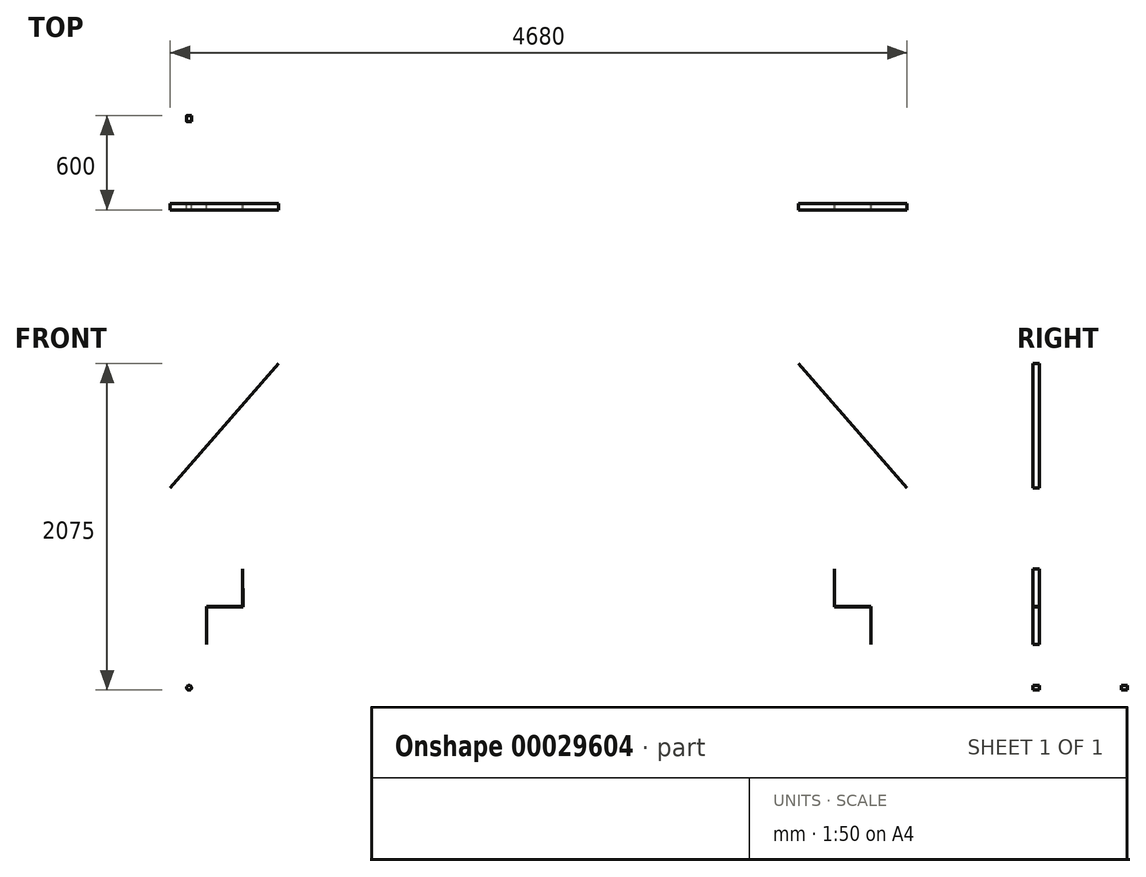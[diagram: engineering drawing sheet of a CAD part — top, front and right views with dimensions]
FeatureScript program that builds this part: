
annotation { "Feature Type Name" : "Feature", "Feature Type Description" : "" }
export const myFeature = defineFeature(function(context is Context, id is Id, definition is map)
    precondition{}
    {
        {
            var Q0;
            Q0=qCreatedBy(makeId("Top.planeOp"),FACE);
            var sketch = newSketch(context, id + "F0", { "sketchPlane" : qUnion([Q0])});
            skLineSegment(sketch, "E0.rect.bottom", {"start": v(1650, 400) * mm, "end": v(-1650, 400) * mm});
            skLineSegment(sketch, "E0.rect.top", {"start": v(1650, -400) * mm, "end": v(-1650, -400) * mm});
            skLineSegment(sketch, "E0.rect.left", {"start": v(1650, 400) * mm, "end": v(1650, -400) * mm});
            skLineSegment(sketch, "E0.rect.right", {"start": v(-1650, 400) * mm, "end": v(-1650, -400) * mm});
            skPoint(sketch, "E0.rect.middle", {"position": v(0, 0) * mm});
            skLineSegment(sketch, "E1.rect.bottom", {"start": v(1610, 360) * mm, "end": v(-1610, 360) * mm});
            skLineSegment(sketch, "E1.rect.top", {"start": v(1610, -360) * mm, "end": v(-1610, -360) * mm});
            skLineSegment(sketch, "E1.rect.left", {"start": v(1610, 360) * mm, "end": v(1610, -360) * mm});
            skLineSegment(sketch, "E1.rect.right", {"start": v(-1610, 360) * mm, "end": v(-1610, -360) * mm});
            skLineSegment(sketch, "E2", {"start": v(0, 360) * mm, "end": v(0, -360) * mm, "construction": true});
            skLineSegment(sketch, "E3", {"start": v(20, 360) * mm, "end": v(20, -360) * mm});
            skLineSegment(sketch, "E4", {"start": v(-20, 360) * mm, "end": v(-20, -360) * mm});
            skLineSegment(sketch, "E5", {"start": v(1610, -20) * mm, "end": v(-1610, -20) * mm});
            skLineSegment(sketch, "E6.0", {"start": v(1610, 20) * mm, "end": v(-1610, 20) * mm});
            skLineSegment(sketch, "E7", {"start": v(0, 0) * mm, "end": v(1610, 0) * mm, "construction": true});
            skLineSegment(sketch, "E8", {"start": v(0, 0) * mm, "end": v(-1610, 0) * mm, "construction": true});
            skLineSegment(sketch, "E9", {"start": v(805, 0) * mm, "end": v(805, 360) * mm, "construction": true});
            skLineSegment(sketch, "E10", {"start": v(805, 0) * mm, "end": v(805, -360) * mm, "construction": true});
            skLineSegment(sketch, "E11", {"start": v(825, 360) * mm, "end": v(825, -360) * mm});
            skLineSegment(sketch, "E12", {"start": v(785, 360) * mm, "end": v(785, -360) * mm});
            skLineSegment(sketch, "E13.MirrorCS", {"start": v(-785, 360) * mm, "end": v(-785, -360) * mm});
            skLineSegment(sketch, "E14.MirrorCS", {"start": v(-825, 360) * mm, "end": v(-825, -360) * mm});
            skSolve(sketch);
        }
        {
            var Q0;
            Q0=makeQuery(id+"F0.imprint","IMPRINT",FACE,{"disambiguationData":[TD([[makeQuery(id+"F0.imprint","IMPRINT",EDGE,{"derivedFrom":sQuery(id+"F0.wireOp",EDGE,"E0.rect.bottom")}),1.0]])]});
            var Q1;
            {var subQ3=sQuery(id+"F0.wireOp",EDGE,"E1.rect.bottom");var subQ5=sQuery(id+"F0.wireOp",EDGE,"E13.MirrorCS");var subQ7=makeQuery(id+"F0.imprint","INTERSECT",VERTEX,{"derivedFrom":[subQ3,subQ5]});Q1=makeQuery(id+"F0.imprint","IMPRINT",FACE,{"disambiguationData":[TD([[makeQuery(id+"F0.imprint","IMPRINT",EDGE,{"disambiguationData":[TD([[subQ7,-1.0]])],"derivedFrom":subQ3}),1.0]])]});}
            var Q2;
            {var subQ3=sQuery(id+"F0.wireOp",EDGE,"E5");var subQ5=sQuery(id+"F0.wireOp",EDGE,"E13.MirrorCS");var subQ7=makeQuery(id+"F0.imprint","INTERSECT",VERTEX,{"derivedFrom":[subQ3,subQ5]});Q2=makeQuery(id+"F0.imprint","IMPRINT",FACE,{"disambiguationData":[TD([[makeQuery(id+"F0.imprint","IMPRINT",EDGE,{"disambiguationData":[TD([[subQ7,-1.0]])],"derivedFrom":subQ3}),-1.0]])]});}
            var Q3;
            {var subQ0=sQuery(id+"F0.wireOp",EDGE,"E13.MirrorCS");var subQ3=sQuery(id+"F0.wireOp",EDGE,"E1.rect.top");var subQ4=makeQuery(id+"F0.imprint","INTERSECT",VERTEX,{"derivedFrom":[subQ3,subQ0]});Q3=makeQuery(id+"F0.imprint","IMPRINT",FACE,{"disambiguationData":[TD([[makeQuery(id+"F0.imprint","IMPRINT",EDGE,{"disambiguationData":[TD([[subQ4,-1.0]])],"derivedFrom":subQ3}),-1.0]])]});}
            var Q4;
            {var subQ3=sQuery(id+"F0.wireOp",EDGE,"E5");var subQ5=sQuery(id+"F0.wireOp",EDGE,"E1.rect.right");var subQ7=makeQuery(id+"F0.imprint","INTERSECT",VERTEX,{"derivedFrom":[subQ5,subQ3]});Q4=makeQuery(id+"F0.imprint","IMPRINT",FACE,{"disambiguationData":[TD([[makeQuery(id+"F0.imprint","IMPRINT",EDGE,{"disambiguationData":[TD([[subQ7,1.0]])],"derivedFrom":subQ5}),1.0]])]});}
            var Q5;
            {var subQ0=sQuery(id+"F0.wireOp",EDGE,"E6.0");var subQ3=sQuery(id+"F0.wireOp",EDGE,"E4");var subQ4=makeQuery(id+"F0.imprint","INTERSECT",VERTEX,{"derivedFrom":[subQ3,subQ0]});Q5=makeQuery(id+"F0.imprint","IMPRINT",FACE,{"disambiguationData":[TD([[makeQuery(id+"F0.imprint","IMPRINT",EDGE,{"disambiguationData":[TD([[subQ4,-1.0]])],"derivedFrom":subQ3}),-1.0]])]});}
            var Q6;
            {var subQ3=sQuery(id+"F0.wireOp",EDGE,"E3");var subQ5=sQuery(id+"F0.wireOp",EDGE,"E1.rect.top");var subQ6=makeQuery(id+"F0.imprint","INTERSECT",VERTEX,{"derivedFrom":[subQ5,subQ3]});Q6=makeQuery(id+"F0.imprint","IMPRINT",FACE,{"disambiguationData":[TD([[makeQuery(id+"F0.imprint","IMPRINT",EDGE,{"disambiguationData":[TD([[subQ6,-1.0]])],"derivedFrom":subQ5}),-1.0]])]});}
            var Q7;
            {var subQ3=sQuery(id+"F0.wireOp",EDGE,"E1.rect.bottom");var subQ5=sQuery(id+"F0.wireOp",EDGE,"E3");var subQ7=makeQuery(id+"F0.imprint","INTERSECT",VERTEX,{"derivedFrom":[subQ3,subQ5]});Q7=makeQuery(id+"F0.imprint","IMPRINT",FACE,{"disambiguationData":[TD([[makeQuery(id+"F0.imprint","IMPRINT",EDGE,{"disambiguationData":[TD([[subQ7,-1.0]])],"derivedFrom":subQ3}),1.0]])]});}
            var Q8;
            {var subQ3=sQuery(id+"F0.wireOp",EDGE,"E5");var subQ5=sQuery(id+"F0.wireOp",EDGE,"E1.rect.left");var subQ6=makeQuery(id+"F0.imprint","INTERSECT",VERTEX,{"derivedFrom":[subQ5,subQ3]});Q8=makeQuery(id+"F0.imprint","IMPRINT",FACE,{"disambiguationData":[TD([[makeQuery(id+"F0.imprint","IMPRINT",EDGE,{"disambiguationData":[TD([[subQ6,1.0]])],"derivedFrom":subQ5}),-1.0]])]});}
            var Q9;
            {var subQ3=sQuery(id+"F0.wireOp",EDGE,"E1.rect.top");var subQ5=sQuery(id+"F0.wireOp",EDGE,"E11");var subQ7=makeQuery(id+"F0.imprint","INTERSECT",VERTEX,{"derivedFrom":[subQ3,subQ5]});Q9=makeQuery(id+"F0.imprint","IMPRINT",FACE,{"disambiguationData":[TD([[makeQuery(id+"F0.imprint","IMPRINT",EDGE,{"disambiguationData":[TD([[subQ7,-1.0]])],"derivedFrom":subQ3}),-1.0]])]});}
            var Q10;
            {var subQ1=sQuery(id+"F0.wireOp",EDGE,"E6.0");var subQ5=sQuery(id+"F0.wireOp",EDGE,"E3");var subQ6=makeQuery(id+"F0.imprint","INTERSECT",VERTEX,{"derivedFrom":[subQ5,subQ1]});Q10=makeQuery(id+"F0.imprint","IMPRINT",FACE,{"disambiguationData":[TD([[makeQuery(id+"F0.imprint","IMPRINT",EDGE,{"disambiguationData":[TD([[subQ6,-1.0]])],"derivedFrom":subQ5}),1.0]])]});}
            var Q11;
            {var subQ3=sQuery(id+"F0.wireOp",EDGE,"E1.rect.bottom");var subQ5=sQuery(id+"F0.wireOp",EDGE,"E11");var subQ7=makeQuery(id+"F0.imprint","INTERSECT",VERTEX,{"derivedFrom":[subQ3,subQ5]});Q11=makeQuery(id+"F0.imprint","IMPRINT",FACE,{"disambiguationData":[TD([[makeQuery(id+"F0.imprint","IMPRINT",EDGE,{"disambiguationData":[TD([[subQ7,-1.0]])],"derivedFrom":subQ3}),1.0]])]});}
            var Q12;
            {var subQ0=sQuery(id+"F0.wireOp",EDGE,"E11");var subQ3=sQuery(id+"F0.wireOp",EDGE,"E5");var subQ4=makeQuery(id+"F0.imprint","INTERSECT",VERTEX,{"derivedFrom":[subQ3,subQ0]});Q12=makeQuery(id+"F0.imprint","IMPRINT",FACE,{"disambiguationData":[TD([[makeQuery(id+"F0.imprint","IMPRINT",EDGE,{"disambiguationData":[TD([[subQ4,-1.0]])],"derivedFrom":subQ3}),-1.0]])]});}
            var Q13;
            {var subQ3=sQuery(id+"F0.wireOp",EDGE,"E3");var subQ5=sQuery(id+"F0.wireOp",EDGE,"E6.0");var subQ7=makeQuery(id+"F0.imprint","INTERSECT",VERTEX,{"derivedFrom":[subQ3,subQ5]});Q13=makeQuery(id+"F0.imprint","IMPRINT",FACE,{"disambiguationData":[TD([[makeQuery(id+"F0.imprint","IMPRINT",EDGE,{"disambiguationData":[TD([[subQ7,-1.0]])],"derivedFrom":subQ3}),-1.0]])]});}
            extrude(context, id + "F1", {"entities" : qUnion([Q0, Q1, Q2, Q3, Q4, Q5, Q6, Q7, Q8, Q9, Q10, Q11, Q12, Q13]), "depth" : 25 * mm});
        }
        {
            var Q0;
            Q0=makeQuery(id+"F1.opExtrude","CAP_FACE",FACE,{"disambiguationData":[OSD([sQuery(id+"F0.wireOp",EDGE,"E0.rect.bottom"),sQuery(id+"F0.wireOp",EDGE,"E0.rect.top"),sQuery(id+"F0.wireOp",EDGE,"E0.rect.left"),sQuery(id+"F0.wireOp",EDGE,"E0.rect.right"),sQuery(id+"F0.wireOp",EDGE,"E1.rect.bottom"),sQuery(id+"F0.wireOp",EDGE,"E1.rect.top"),sQuery(id+"F0.wireOp",EDGE,"E1.rect.left"),sQuery(id+"F0.wireOp",EDGE,"E1.rect.right"),sQuery(id+"F0.wireOp",EDGE,"E3"),sQuery(id+"F0.wireOp",EDGE,"E4"),sQuery(id+"F0.wireOp",EDGE,"E5"),sQuery(id+"F0.wireOp",EDGE,"E6.0"),sQuery(id+"F0.wireOp",EDGE,"E11"),sQuery(id+"F0.wireOp",EDGE,"E12"),sQuery(id+"F0.wireOp",EDGE,"E13.MirrorCS"),sQuery(id+"F0.wireOp",EDGE,"E14.MirrorCS")])],"isStart":false});
            var sketch = newSketch(context, id + "F2", { "sketchPlane" : qUnion([Q0])});
            skLineSegment(sketch, "E15.bottom", {"start": v(-1650, 400) * mm, "end": v(-1610, 400) * mm});
            skLineSegment(sketch, "E15.top", {"start": v(-1650, 360) * mm, "end": v(-1610, 360) * mm});
            skLineSegment(sketch, "E15.left", {"start": v(-1650, 400) * mm, "end": v(-1650, 360) * mm});
            skLineSegment(sketch, "E15.right", {"start": v(-1610, 400) * mm, "end": v(-1610, 360) * mm});
            skLineSegment(sketch, "E16.bottom", {"start": v(-1650, -400) * mm, "end": v(-1610, -400) * mm});
            skLineSegment(sketch, "E16.top", {"start": v(-1650, -360) * mm, "end": v(-1610, -360) * mm});
            skLineSegment(sketch, "E16.left", {"start": v(-1650, -400) * mm, "end": v(-1650, -360) * mm});
            skLineSegment(sketch, "E16.right", {"start": v(-1610, -400) * mm, "end": v(-1610, -360) * mm});
            skLineSegment(sketch, "E17.bottom", {"start": v(-825, -360) * mm, "end": v(-785, -360) * mm});
            skLineSegment(sketch, "E17.top", {"start": v(-825, -400) * mm, "end": v(-785, -400) * mm});
            skLineSegment(sketch, "E17.left", {"start": v(-825, -360) * mm, "end": v(-825, -400) * mm});
            skLineSegment(sketch, "E17.right", {"start": v(-785, -360) * mm, "end": v(-785, -400) * mm});
            skLineSegment(sketch, "E18.bottom", {"start": v(-20, -360) * mm, "end": v(20, -360) * mm});
            skLineSegment(sketch, "E18.top", {"start": v(-20, -400) * mm, "end": v(20, -400) * mm});
            skLineSegment(sketch, "E18.left", {"start": v(-20, -360) * mm, "end": v(-20, -400) * mm});
            skLineSegment(sketch, "E18.right", {"start": v(20, -360) * mm, "end": v(20, -400) * mm});
            skPoint(sketch, "E19.oppositeSnap0", {"position": v(20, 190) * mm});
            skLineSegment(sketch, "E19.bottom", {"start": v(-20, 360) * mm, "end": v(20, 360) * mm});
            skLineSegment(sketch, "E19.top", {"start": v(-20, 400) * mm, "end": v(20, 400) * mm});
            skLineSegment(sketch, "E19.left", {"start": v(-20, 360) * mm, "end": v(-20, 400) * mm});
            skLineSegment(sketch, "E19.right", {"start": v(20, 360) * mm, "end": v(20, 400) * mm});
            skLineSegment(sketch, "E20.bottom", {"start": v(-825, 360) * mm, "end": v(-785, 360) * mm});
            skLineSegment(sketch, "E20.top", {"start": v(-825, 400) * mm, "end": v(-785, 400) * mm});
            skLineSegment(sketch, "E20.left", {"start": v(-825, 360) * mm, "end": v(-825, 400) * mm});
            skLineSegment(sketch, "E20.right", {"start": v(-785, 360) * mm, "end": v(-785, 400) * mm});
            skLineSegment(sketch, "E21.bottom", {"start": v(785, 360) * mm, "end": v(825, 360) * mm});
            skLineSegment(sketch, "E21.top", {"start": v(785, 400) * mm, "end": v(825, 400) * mm});
            skLineSegment(sketch, "E21.left", {"start": v(785, 360) * mm, "end": v(785, 400) * mm});
            skLineSegment(sketch, "E21.right", {"start": v(825, 360) * mm, "end": v(825, 400) * mm});
            skLineSegment(sketch, "E22.bottom", {"start": v(785, -360) * mm, "end": v(825, -360) * mm});
            skLineSegment(sketch, "E22.top", {"start": v(785, -400) * mm, "end": v(825, -400) * mm});
            skLineSegment(sketch, "E22.left", {"start": v(785, -360) * mm, "end": v(785, -400) * mm});
            skLineSegment(sketch, "E22.right", {"start": v(825, -360) * mm, "end": v(825, -400) * mm});
            skLineSegment(sketch, "E23.bottom", {"start": v(1610, -360) * mm, "end": v(1650, -360) * mm});
            skLineSegment(sketch, "E23.top", {"start": v(1610, -400) * mm, "end": v(1650, -400) * mm});
            skLineSegment(sketch, "E23.left", {"start": v(1610, -360) * mm, "end": v(1610, -400) * mm});
            skLineSegment(sketch, "E23.right", {"start": v(1650, -360) * mm, "end": v(1650, -400) * mm});
            skLineSegment(sketch, "E24.bottom", {"start": v(1610, 360) * mm, "end": v(1650, 360) * mm});
            skLineSegment(sketch, "E24.top", {"start": v(1610, 400) * mm, "end": v(1650, 400) * mm});
            skLineSegment(sketch, "E24.left", {"start": v(1610, 360) * mm, "end": v(1610, 400) * mm});
            skLineSegment(sketch, "E24.right", {"start": v(1650, 360) * mm, "end": v(1650, 400) * mm});
            skLineSegment(sketch, "E25.bottom", {"start": v(-1650, -160) * mm, "end": v(-1610, -160) * mm});
            skLineSegment(sketch, "E25.top", {"start": v(-1650, -200) * mm, "end": v(-1610, -200) * mm});
            skLineSegment(sketch, "E25.left", {"start": v(-1650, -160) * mm, "end": v(-1650, -200) * mm});
            skLineSegment(sketch, "E25.right", {"start": v(-1610, -160) * mm, "end": v(-1610, -200) * mm});
            skLineSegment(sketch, "E26.MirrorCS", {"start": v(1650, -200) * mm, "end": v(1610, -200) * mm});
            skLineSegment(sketch, "E27.MirrorCS", {"start": v(1650, -160) * mm, "end": v(1650, -200) * mm});
            skLineSegment(sketch, "E28.MirrorCS", {"start": v(1650, -160) * mm, "end": v(1610, -160) * mm});
            skLineSegment(sketch, "E29.MirrorCS", {"start": v(1610, -160) * mm, "end": v(1610, -200) * mm});
            skSolve(sketch);
        }
        {
            var Q0;
            Q0=makeQuery(id+"F2.imprint","IMPRINT",FACE,{"disambiguationData":[TD([[makeQuery(id+"F2.imprint","IMPRINT",EDGE,{"derivedFrom":sQuery(id+"F2.wireOp",EDGE,"E15.bottom")}),1.0]])]});
            var Q1;
            Q1=makeQuery(id+"F2.imprint","IMPRINT",FACE,{"disambiguationData":[TD([[makeQuery(id+"F2.imprint","IMPRINT",EDGE,{"derivedFrom":sQuery(id+"F2.wireOp",EDGE,"E24.bottom")}),1.0]])]});
            var Q2;
            Q2=makeQuery(id+"F2.imprint","IMPRINT",FACE,{"disambiguationData":[TD([[makeQuery(id+"F2.imprint","IMPRINT",EDGE,{"derivedFrom":sQuery(id+"F2.wireOp",EDGE,"E26.MirrorCS")}),-1.0]])]});
            var Q3;
            Q3=makeQuery(id+"F2.imprint","IMPRINT",FACE,{"disambiguationData":[TD([[makeQuery(id+"F2.imprint","IMPRINT",EDGE,{"derivedFrom":sQuery(id+"F2.wireOp",EDGE,"E25.bottom")}),-1.0]])]});
            extrude(context, id + "F3", {"entities" : qUnion([Q0, Q1, Q2, Q3]), "operationType" : NewBodyOperationType.ADD, "depth" : 1000 * mm, "hasSecondDirection" : true, "secondDirectionOppositeDirection" : true, "secondDirectionDepth" : 1040 * mm});
        }
        {
            var Q0;
            Q0=makeQuery(id+"F2.imprint","IMPRINT",FACE,{"disambiguationData":[TD([[makeQuery(id+"F2.imprint","IMPRINT",EDGE,{"derivedFrom":sQuery(id+"F2.wireOp",EDGE,"E17.bottom")}),-1.0]])]});
            var Q1;
            Q1=makeQuery(id+"F2.imprint","IMPRINT",FACE,{"disambiguationData":[TD([[makeQuery(id+"F2.imprint","IMPRINT",EDGE,{"derivedFrom":sQuery(id+"F2.wireOp",EDGE,"E19.bottom")}),1.0]])]});
            var Q2;
            Q2=makeQuery(id+"F2.imprint","IMPRINT",FACE,{"disambiguationData":[TD([[makeQuery(id+"F2.imprint","IMPRINT",EDGE,{"derivedFrom":sQuery(id+"F2.wireOp",EDGE,"E18.bottom")}),-1.0]])]});
            var Q3;
            Q3=makeQuery(id+"F2.imprint","IMPRINT",FACE,{"disambiguationData":[TD([[makeQuery(id+"F2.imprint","IMPRINT",EDGE,{"derivedFrom":sQuery(id+"F2.wireOp",EDGE,"E20.bottom")}),1.0]])]});
            var Q4;
            Q4=makeQuery(id+"F2.imprint","IMPRINT",FACE,{"disambiguationData":[TD([[makeQuery(id+"F2.imprint","IMPRINT",EDGE,{"derivedFrom":sQuery(id+"F2.wireOp",EDGE,"E21.bottom")}),1.0]])]});
            var Q5;
            Q5=makeQuery(id+"F2.imprint","IMPRINT",FACE,{"disambiguationData":[TD([[makeQuery(id+"F2.imprint","IMPRINT",EDGE,{"derivedFrom":sQuery(id+"F2.wireOp",EDGE,"E22.bottom")}),-1.0]])]});
            var Q6;
            Q6=makeQuery(id+"F2.imprint","IMPRINT",FACE,{"disambiguationData":[TD([[makeQuery(id+"F2.imprint","IMPRINT",EDGE,{"derivedFrom":sQuery(id+"F2.wireOp",EDGE,"E16.bottom")}),-1.0]])]});
            var Q7;
            Q7=makeQuery(id+"F2.imprint","IMPRINT",FACE,{"disambiguationData":[TD([[makeQuery(id+"F2.imprint","IMPRINT",EDGE,{"derivedFrom":sQuery(id+"F2.wireOp",EDGE,"E23.bottom")}),-1.0]])]});
            extrude(context, id + "F4", {"entities" : qUnion([Q0, Q1, Q2, Q3, Q4, Q5, Q6, Q7]), "operationType" : NewBodyOperationType.ADD, "depth" : 1000 * mm});
        }
        {
            var Q0;
            Q0=makeQuery(id+"F4.boolean.opBoolean","MERGE",FACE,{"derivedFrom":[makeQuery(id+"F3.boolean.opBoolean","MERGE",FACE,{"derivedFrom":[makeQuery(id+"F1.opExtrude","SWEPT_FACE",FACE,{"disambiguationData":[OSD([sQuery(id+"F0.wireOp",EDGE,"E0.rect.left")])]}),makeQuery(id+"F3.opExtrude","SWEPT_FACE",FACE,{"disambiguationData":[OSD([sQuery(id+"F2.wireOp",EDGE,"E24.right")])]}),makeQuery(id+"F3.opExtrude","SWEPT_FACE",FACE,{"disambiguationData":[OSD([sQuery(id+"F2.wireOp",EDGE,"E27.MirrorCS")])]})]}),makeQuery(id+"F4.opExtrude","SWEPT_FACE",FACE,{"disambiguationData":[OSD([sQuery(id+"F2.wireOp",EDGE,"E23.right")])]})]});
            var sketch = newSketch(context, id + "F5", { "sketchPlane" : qUnion([Q0])});
            skLineSegment(sketch, "E30.bottom", {"start": v(-400, 1025) * mm, "end": v(-360, 1025) * mm});
            skLineSegment(sketch, "E30.top", {"start": v(-400, 1065) * mm, "end": v(-360, 1065) * mm});
            skLineSegment(sketch, "E30.left", {"start": v(-400, 1025) * mm, "end": v(-400, 1065) * mm});
            skLineSegment(sketch, "E30.right", {"start": v(-360, 1025) * mm, "end": v(-360, 1065) * mm});
            skLineSegment(sketch, "E31.MirrorCS", {"start": v(400, 1025) * mm, "end": v(360, 1025) * mm});
            skLineSegment(sketch, "E32.MirrorCS", {"start": v(360, 1025) * mm, "end": v(360, 1065) * mm});
            skLineSegment(sketch, "E33.MirrorCS", {"start": v(400, 1065) * mm, "end": v(360, 1065) * mm});
            skLineSegment(sketch, "E34.MirrorCS", {"start": v(400, 1025) * mm, "end": v(400, 1065) * mm});
            skSolve(sketch);
        }
        {
            var Q0;
            Q0 = qSketchRegion(id + "F5", true);
            extrude(context, id + "F6", {"entities" : qUnion([Q0]), "operationType" : NewBodyOperationType.ADD, "oppositeDirection" : true, "depth" : 3300 * mm});
        }
        {
            var Q0;
            Q0=makeQuery(id+"F3.opExtrude","CAP_FACE",FACE,{"disambiguationData":[OSD([sQuery(id+"F2.wireOp",EDGE,"E15.bottom"),sQuery(id+"F2.wireOp",EDGE,"E15.top"),sQuery(id+"F2.wireOp",EDGE,"E15.left"),sQuery(id+"F2.wireOp",EDGE,"E15.right")])],"isStart":true});
            var sketch = newSketch(context, id + "F7", { "sketchPlane" : qUnion([Q0])});
            skLineSegment(sketch, "E35.bottom", {"start": v(-1610, -400) * mm, "end": v(-2340, -400) * mm});
            skLineSegment(sketch, "E35.top", {"start": v(-1610, 200) * mm, "end": v(-2340, 200) * mm});
            skLineSegment(sketch, "E35.left", {"start": v(-1610, -400) * mm, "end": v(-1610, 200) * mm});
            skLineSegment(sketch, "E35.right", {"start": v(-2340, -400) * mm, "end": v(-2340, 200) * mm});
            skLineSegment(sketch, "E36.bottom", {"start": v(-1650, -360) * mm, "end": v(-2300, -360) * mm});
            skLineSegment(sketch, "E36.top", {"start": v(-1650, 160) * mm, "end": v(-2300, 160) * mm});
            skLineSegment(sketch, "E36.left", {"start": v(-1650, -360) * mm, "end": v(-1650, 160) * mm});
            skLineSegment(sketch, "E36.right", {"start": v(-2300, -360) * mm, "end": v(-2300, 160) * mm});
            skLineSegment(sketch, "E37.MirrorCS", {"start": v(1610, -400) * mm, "end": v(1610, 200) * mm});
            skLineSegment(sketch, "E38.MirrorCS", {"start": v(1650, -360) * mm, "end": v(1650, 160) * mm});
            skLineSegment(sketch, "E39.MirrorCS", {"start": v(1610, 200) * mm, "end": v(2340, 200) * mm});
            skLineSegment(sketch, "E40.MirrorCS", {"start": v(1650, 160) * mm, "end": v(2300, 160) * mm});
            skLineSegment(sketch, "E41.MirrorCS", {"start": v(2300, -360) * mm, "end": v(2300, 160) * mm});
            skLineSegment(sketch, "E42.MirrorCS", {"start": v(2340, -400) * mm, "end": v(2340, 200) * mm});
            skLineSegment(sketch, "E43.MirrorCS", {"start": v(1610, -400) * mm, "end": v(2340, -400) * mm});
            skLineSegment(sketch, "E44.MirrorCS", {"start": v(1650, -360) * mm, "end": v(2300, -360) * mm});
            skSolve(sketch);
        }
        {
            var Q0;
            {var subQ1=makeQuery(id+"F3.opExtrude","CAP_EDGE",EDGE,{"disambiguationData":[OSD([sQuery(id+"F2.wireOp",EDGE,"E15.top")])],"isStart":true});Q0=makeQuery(id+"F7.imprint","IMPRINT",FACE,{"disambiguationData":[TD([[makeQuery(id+"F7.imprint","IMPRINT",EDGE,{"derivedFrom":subQ1}),-1.0]])]});}
            var Q1;
            {var subQ4=sQuery(id+"F7.wireOp",EDGE,"E35.top");Q1=makeQuery(id+"F7.imprint","IMPRINT",FACE,{"disambiguationData":[TD([[makeQuery(id+"F7.imprint","IMPRINT",EDGE,{"derivedFrom":subQ4}),1.0]])]});}
            var Q2;
            Q2=makeQuery(id+"F7.imprint","IMPRINT",FACE,{"disambiguationData":[TD([[makeQuery(id+"F7.imprint","IMPRINT",EDGE,{"derivedFrom":sQuery(id+"F7.wireOp",EDGE,"E37.MirrorCS")}),-1.0]])]});
            extrude(context, id + "F8", {"entities" : qUnion([Q0, Q1, Q2]), "operationType" : NewBodyOperationType.ADD, "oppositeDirection" : true, "depth" : 40 * mm});
        }
        {
            var Q0;
            {var subQ0=sQuery(id+"F7.wireOp",EDGE,"E35.bottom");var subQ1=sQuery(id+"F7.wireOp",EDGE,"E35.top");var subQ2=sQuery(id+"F7.wireOp",EDGE,"E35.right");var subQ3=sQuery(id+"F7.wireOp",EDGE,"E36.bottom");var subQ4=sQuery(id+"F7.wireOp",EDGE,"E36.top");var subQ5=sQuery(id+"F7.wireOp",EDGE,"E36.left");var subQ6=sQuery(id+"F7.wireOp",EDGE,"E36.right");var subQ7=makeQuery(id+"F8.opExtrude","CAP_FACE",FACE,{"disambiguationData":[OSD([subQ0,subQ1,sQuery(id+"F7.wireOp",EDGE,"E35.left"),subQ2,subQ3,subQ4,subQ5,subQ6])],"isStart":false});Q0=makeQuery(id+"F8.boolean.opBoolean","SPLIT",FACE,{"disambiguationData":[TD([makeQuery(id+"F1.opExtrude","SWEPT_FACE",FACE,{"disambiguationData":[OSD([sQuery(id+"F0.wireOp",EDGE,"E0.rect.bottom")])]})])],"derivedFrom":subQ7});}
            var sketch = newSketch(context, id + "F9", { "sketchPlane" : qUnion([Q0])});
            skLineSegment(sketch, "E45.bottom", {"start": v(-2340, 400) * mm, "end": v(-2300, 400) * mm});
            skLineSegment(sketch, "E45.top", {"start": v(-2340, 360) * mm, "end": v(-2300, 360) * mm});
            skLineSegment(sketch, "E45.left", {"start": v(-2340, 400) * mm, "end": v(-2340, 360) * mm});
            skLineSegment(sketch, "E45.right", {"start": v(-2300, 400) * mm, "end": v(-2300, 360) * mm});
            skLineSegment(sketch, "E46.bottom", {"start": v(-2340, -200) * mm, "end": v(-2300, -200) * mm});
            skLineSegment(sketch, "E46.top", {"start": v(-2340, -160) * mm, "end": v(-2300, -160) * mm});
            skLineSegment(sketch, "E46.left", {"start": v(-2340, -200) * mm, "end": v(-2340, -160) * mm});
            skLineSegment(sketch, "E46.right", {"start": v(-2300, -200) * mm, "end": v(-2300, -160) * mm});
            skLineSegment(sketch, "E47.MirrorCS", {"start": v(2340, 360) * mm, "end": v(2300, 360) * mm});
            skLineSegment(sketch, "E48.MirrorCS", {"start": v(2340, 400) * mm, "end": v(2340, 360) * mm});
            skLineSegment(sketch, "E49.MirrorCS", {"start": v(2340, 400) * mm, "end": v(2300, 400) * mm});
            skLineSegment(sketch, "E50.MirrorCS", {"start": v(2300, 400) * mm, "end": v(2300, 360) * mm});
            skLineSegment(sketch, "E51.MirrorCS", {"start": v(2340, -160) * mm, "end": v(2300, -160) * mm});
            skLineSegment(sketch, "E52.MirrorCS", {"start": v(2300, -200) * mm, "end": v(2300, -160) * mm});
            skLineSegment(sketch, "E53.MirrorCS", {"start": v(2340, -200) * mm, "end": v(2300, -200) * mm});
            skLineSegment(sketch, "E54.MirrorCS", {"start": v(2340, -200) * mm, "end": v(2340, -160) * mm});
            skSolve(sketch);
        }
        {
            var Q0;
            Q0 = qSketchRegion(id + "F9", true);
            extrude(context, id + "F10", {"entities" : qUnion([Q0]), "operationType" : NewBodyOperationType.ADD, "depth" : 1250 * mm});
        }
        {
            var Q0;
            {var subQ0=sQuery(id+"F2.wireOp",EDGE,"E25.top");var subQ1=sQuery(id+"F2.wireOp",EDGE,"E25.right");var subQ2=sQuery(id+"F2.wireOp",EDGE,"E25.left");Q0=makeQuery(id+"F10.boolean.opBoolean","MERGE",FACE,{"derivedFrom":[makeQuery(id+"F8.boolean.opBoolean","MERGE",FACE,{"derivedFrom":[makeQuery(id+"F3.boolean.opBoolean","SPLIT",FACE,{"disambiguationData":[TD([makeQuery(id+"F3.opExtrude","CAP_FACE",FACE,{"disambiguationData":[OSD([sQuery(id+"F2.wireOp",EDGE,"E25.bottom"),subQ0,subQ2,subQ1])],"isStart":true})])],"derivedFrom":makeQuery(id+"F3.opExtrude","SWEPT_FACE",FACE,{"disambiguationData":[OSD([subQ0])]})}),makeQuery(id+"F8.opExtrude","SWEPT_FACE",FACE,{"disambiguationData":[OSD([sQuery(id+"F7.wireOp",EDGE,"E35.top")])]})]}),makeQuery(id+"F10.opExtrude","SWEPT_FACE",FACE,{"disambiguationData":[OSD([sQuery(id+"F9.wireOp",EDGE,"E46.bottom")])]})]});}
            var sketch = newSketch(context, id + "F11", { "sketchPlane" : qUnion([Q0])});
            skLineSegment(sketch, "E55", {"start": v(-1650, -240) * mm, "end": v(-1880, -240) * mm});
            skLineSegment(sketch, "E56", {"start": v(-1880, -240) * mm, "end": v(-1880, -480) * mm});
            skLineSegment(sketch, "E57", {"start": v(-1880, -480) * mm, "end": v(-2110, -480) * mm});
            skLineSegment(sketch, "E58", {"start": v(-2110, -480) * mm, "end": v(-2110, -720) * mm});
            skLineSegment(sketch, "E59", {"start": v(-2110, -720) * mm, "end": v(-2300, -720) * mm});
            skLineSegment(sketch, "E60.0", {"start": v(-2070, -760) * mm, "end": v(-2300, -760) * mm});
            skLineSegment(sketch, "E60.1", {"start": v(-1650, -280) * mm, "end": v(-1840, -280) * mm});
            skLineSegment(sketch, "E60.2", {"start": v(-1840, -280) * mm, "end": v(-1840, -520) * mm});
            skLineSegment(sketch, "E60.3", {"start": v(-1840, -520) * mm, "end": v(-2070, -520) * mm});
            skLineSegment(sketch, "E60.4", {"start": v(-2070, -520) * mm, "end": v(-2070, -760) * mm});
            skLineSegment(sketch, "E61", {"start": v(-1650, -240) * mm, "end": v(-1650, -280) * mm});
            skLineSegment(sketch, "E62", {"start": v(-2300, -720) * mm, "end": v(-2300, -760) * mm});
            skLineSegment(sketch, "E63.MirrorCS", {"start": v(1650, -240) * mm, "end": v(1650, -280) * mm});
            skLineSegment(sketch, "E64.MirrorCS", {"start": v(1650, -280) * mm, "end": v(1840, -280) * mm});
            skLineSegment(sketch, "E65.MirrorCS", {"start": v(1880, -240) * mm, "end": v(1880, -480) * mm});
            skLineSegment(sketch, "E66.MirrorCS", {"start": v(1650, -240) * mm, "end": v(1880, -240) * mm});
            skLineSegment(sketch, "E67.MirrorCS", {"start": v(2300, -720) * mm, "end": v(2300, -760) * mm});
            skLineSegment(sketch, "E68.MirrorCS", {"start": v(1880, -480) * mm, "end": v(2110, -480) * mm});
            skLineSegment(sketch, "E69.MirrorCS", {"start": v(2110, -480) * mm, "end": v(2110, -720) * mm});
            skLineSegment(sketch, "E70.MirrorCS", {"start": v(2110, -720) * mm, "end": v(2300, -720) * mm});
            skLineSegment(sketch, "E71.MirrorCS", {"start": v(2070, -760) * mm, "end": v(2300, -760) * mm});
            skLineSegment(sketch, "E72.MirrorCS", {"start": v(1840, -520) * mm, "end": v(2070, -520) * mm});
            skLineSegment(sketch, "E73.MirrorCS", {"start": v(2070, -520) * mm, "end": v(2070, -760) * mm});
            skLineSegment(sketch, "E74.MirrorCS", {"start": v(1840, -280) * mm, "end": v(1840, -520) * mm});
            skSolve(sketch);
        }
        {
            var Q0;
            Q0=makeQuery(id+"F11.imprint","IMPRINT",FACE,{"disambiguationData":[TD([[makeQuery(id+"F11.imprint","IMPRINT",EDGE,{"derivedFrom":sQuery(id+"F11.wireOp",EDGE,"E55")}),1.0]])]});
            var Q1;
            Q1=makeQuery(id+"F11.imprint","IMPRINT",FACE,{"disambiguationData":[TD([[makeQuery(id+"F11.imprint","IMPRINT",EDGE,{"derivedFrom":sQuery(id+"F11.wireOp",EDGE,"E63.MirrorCS")}),1.0]])]});
            extrude(context, id + "F12", {"entities" : qUnion([Q0, Q1]), "operationType" : NewBodyOperationType.ADD, "oppositeDirection" : true, "depth" : 40 * mm});
        }
        {
            var Q0;
            Q0=makeQuery(id+"F4.opExtrude","SWEPT_FACE",FACE,{"disambiguationData":[OSD([sQuery(id+"F2.wireOp",EDGE,"E16.right")])]});
            var sketch = newSketch(context, id + "F13", { "sketchPlane" : qUnion([Q0])});
            skLineSegment(sketch, "E75.bottom", {"start": v(-400, 565) * mm, "end": v(-360, 565) * mm});
            skLineSegment(sketch, "E75.top", {"start": v(-400, 525) * mm, "end": v(-360, 525) * mm});
            skLineSegment(sketch, "E75.left", {"start": v(-400, 565) * mm, "end": v(-400, 525) * mm});
            skLineSegment(sketch, "E75.right", {"start": v(-360, 565) * mm, "end": v(-360, 525) * mm});
            skLineSegment(sketch, "E76.MirrorCS", {"start": v(400, 525) * mm, "end": v(360, 525) * mm});
            skLineSegment(sketch, "E77.MirrorCS", {"start": v(400, 565) * mm, "end": v(360, 565) * mm});
            skLineSegment(sketch, "E78.MirrorCS", {"start": v(360, 565) * mm, "end": v(360, 525) * mm});
            skLineSegment(sketch, "E79.MirrorCS", {"start": v(400, 565) * mm, "end": v(400, 525) * mm});
            skSolve(sketch);
        }
        {
            var Q0;
            Q0=makeQuery(id+"F13.imprint","IMPRINT",FACE,{"disambiguationData":[TD([[makeQuery(id+"F13.imprint","IMPRINT",EDGE,{"derivedFrom":sQuery(id+"F13.wireOp",EDGE,"E75.bottom")}),-1.0]])]});
            var Q1;
            Q1=makeQuery(id+"F13.imprint","IMPRINT",FACE,{"disambiguationData":[TD([[makeQuery(id+"F13.imprint","IMPRINT",EDGE,{"derivedFrom":sQuery(id+"F13.wireOp",EDGE,"E76.MirrorCS")}),-1.0]])]});
            var Q2;
            Q2=makeQuery(id+"F4.opExtrude","SWEPT_FACE",FACE,{"disambiguationData":[OSD([sQuery(id+"F2.wireOp",EDGE,"E23.left")])]});
            extrude(context, id + "F14", {"entities" : qUnion([Q0, Q1]), "operationType" : NewBodyOperationType.ADD, "endBound" : BoundingType.UP_TO_SURFACE, "endBoundEntityFace" : qUnion([Q2]), "depth" : 25 * mm});
        }
        {
            var Q0;
            Q0=makeQuery(id+"F3.opExtrude","CAP_FACE",FACE,{"disambiguationData":[OSD([sQuery(id+"F2.wireOp",EDGE,"E26.MirrorCS"),sQuery(id+"F2.wireOp",EDGE,"E27.MirrorCS"),sQuery(id+"F2.wireOp",EDGE,"E28.MirrorCS"),sQuery(id+"F2.wireOp",EDGE,"E29.MirrorCS")])],"isStart":false});
            var sketch = newSketch(context, id + "F15", { "sketchPlane" : qUnion([Q0])});
            skLineSegment(sketch, "E80.bottom", {"start": v(1610, -160) * mm, "end": v(1650, -160) * mm});
            skLineSegment(sketch, "E80.top", {"start": v(1610, -360.22) * mm, "end": v(1650, -360.22) * mm});
            skLineSegment(sketch, "E80.left", {"start": v(1610, -160) * mm, "end": v(1610, -360.22) * mm});
            skLineSegment(sketch, "E80.right", {"start": v(1650, -160) * mm, "end": v(1650, -360.22) * mm});
            skLineSegment(sketch, "E81.bottom", {"start": v(1650, -360.22) * mm, "end": v(1650, -399.55) * mm});
            skLineSegment(sketch, "E82.MirrorCS", {"start": v(-1650, -160) * mm, "end": v(-1650, -360.22) * mm});
            skLineSegment(sketch, "E83.MirrorCS", {"start": v(-1610, -160) * mm, "end": v(-1610, -360.22) * mm});
            skLineSegment(sketch, "E84.MirrorCS", {"start": v(-1610, -160) * mm, "end": v(-1650, -160) * mm});
            skLineSegment(sketch, "E85", {"start": v(-1610, -360.22) * mm, "end": v(-1650, -360.22) * mm});
            skSolve(sketch);
        }
        {
            var Q0;
            {var subQ2=sQuery(id+"F15.wireOp",EDGE,"E80.top");Q0=makeQuery(id+"F15.imprint","IMPRINT",FACE,{"disambiguationData":[TD([[makeQuery(id+"F15.imprint","IMPRINT",EDGE,{"derivedFrom":subQ2}),1.0]])]});}
            var Q1;
            {var subQ2=sQuery(id+"F15.wireOp",EDGE,"E80.bottom");Q1=makeQuery(id+"F15.imprint","IMPRINT",FACE,{"disambiguationData":[TD([[makeQuery(id+"F15.imprint","IMPRINT",EDGE,{"derivedFrom":subQ2}),1.0]])]});}
            var Q2;
            Q2=makeQuery(id+"F3.opExtrude","CAP_FACE",FACE,{"disambiguationData":[OSD([sQuery(id+"F2.wireOp",EDGE,"E25.bottom"),sQuery(id+"F2.wireOp",EDGE,"E25.top"),sQuery(id+"F2.wireOp",EDGE,"E25.left"),sQuery(id+"F2.wireOp",EDGE,"E25.right")])],"isStart":false});
            var Q3;
            Q3=makeQuery(id+"F15.imprint","IMPRINT",FACE,{"disambiguationData":[TD([[makeQuery(id+"F15.imprint","IMPRINT",EDGE,{"derivedFrom":sQuery(id+"F15.wireOp",EDGE,"E82.MirrorCS")}),1.0]])]});
            extrude(context, id + "F16", {"entities" : qUnion([Q0, Q1, Q2, Q3]), "operationType" : NewBodyOperationType.ADD, "depth" : 40 * mm});
        }
        {
            var Q0;
            Q0=makeQuery(id+"F14.boolean.opBoolean","MERGE",FACE,{"derivedFrom":[makeQuery(id+"F10.boolean.opBoolean","MERGE",FACE,{"derivedFrom":[makeQuery(id+"F8.boolean.opBoolean","MERGE",FACE,{"derivedFrom":[makeQuery(id+"F6.boolean.opBoolean","MERGE",FACE,{"derivedFrom":[makeQuery(id+"F4.boolean.opBoolean","MERGE",FACE,{"derivedFrom":[makeQuery(id+"F3.boolean.opBoolean","MERGE",FACE,{"derivedFrom":[makeQuery(id+"F1.opExtrude","SWEPT_FACE",FACE,{"disambiguationData":[OSD([sQuery(id+"F0.wireOp",EDGE,"E0.rect.bottom")])]}),makeQuery(id+"F3.opExtrude","SWEPT_FACE",FACE,{"disambiguationData":[OSD([sQuery(id+"F2.wireOp",EDGE,"E15.bottom")])]}),makeQuery(id+"F3.opExtrude","SWEPT_FACE",FACE,{"disambiguationData":[OSD([sQuery(id+"F2.wireOp",EDGE,"E24.top")])]})]}),makeQuery(id+"F4.opExtrude","SWEPT_FACE",FACE,{"disambiguationData":[OSD([sQuery(id+"F2.wireOp",EDGE,"E19.top")])]}),makeQuery(id+"F4.opExtrude","SWEPT_FACE",FACE,{"disambiguationData":[OSD([sQuery(id+"F2.wireOp",EDGE,"E20.top")])]}),makeQuery(id+"F4.opExtrude","SWEPT_FACE",FACE,{"disambiguationData":[OSD([sQuery(id+"F2.wireOp",EDGE,"E21.top")])]})]}),makeQuery(id+"F6.opExtrude","SWEPT_FACE",FACE,{"disambiguationData":[OSD([sQuery(id+"F5.wireOp",EDGE,"E34.MirrorCS")])]})]}),makeQuery(id+"F8.opExtrude","SWEPT_FACE",FACE,{"disambiguationData":[OSD([sQuery(id+"F7.wireOp",EDGE,"E35.bottom")])]}),makeQuery(id+"F8.opExtrude","SWEPT_FACE",FACE,{"disambiguationData":[OSD([sQuery(id+"F7.wireOp",EDGE,"E43.MirrorCS")])]})]}),makeQuery(id+"F10.opExtrude","SWEPT_FACE",FACE,{"disambiguationData":[OSD([sQuery(id+"F9.wireOp",EDGE,"E45.bottom")])]}),makeQuery(id+"F10.opExtrude","SWEPT_FACE",FACE,{"disambiguationData":[OSD([sQuery(id+"F9.wireOp",EDGE,"E49.MirrorCS")])]})]}),makeQuery(id+"F14.opExtrude","SWEPT_FACE",FACE,{"disambiguationData":[OSD([sQuery(id+"F13.wireOp",EDGE,"E79.MirrorCS")])]})]});
            var sketch = newSketch(context, id + "F17", { "sketchPlane" : qUnion([Q0])});
            skLineSegment(sketch, "E86", {"start": v(1627.22, -280) * mm, "end": v(1838.28, -280) * mm});
            skLineSegment(sketch, "E87", {"start": v(1838.28, -523.02) * mm, "end": v(2068.68, -523.02) * mm});
            skLineSegment(sketch, "E88", {"start": v(2068.68, -523.02) * mm, "end": v(2068.68, -780.57) * mm});
            skLineSegment(sketch, "E89", {"start": v(2110, -483.02) * mm, "end": v(1878.26, -483.02) * mm});
            skLineSegment(sketch, "E90", {"start": v(1627.22, -240) * mm, "end": v(1879, -240) * mm});
            skLineSegment(sketch, "E91", {"start": v(1838.28, -280) * mm, "end": v(1838.28, -523.02) * mm});
            skLineSegment(sketch, "E92", {"start": v(1879, -240) * mm, "end": v(1878.26, -483.02) * mm});
            skLineSegment(sketch, "E93", {"start": v(2049.9, -760) * mm, "end": v(2068.68, -780.57) * mm});
            skLineSegment(sketch, "E94", {"start": v(2109.5, -720) * mm, "end": v(2110, -483.02) * mm});
            skLineSegment(sketch, "E95", {"start": v(1627.22, -240) * mm, "end": v(1627.22, -280) * mm});
            skPoint(sketch, "E96.orphan", {"position": v(1650, -240) * mm});
            skPoint(sketch, "E97.orphan", {"position": v(1650, -280) * mm});
            skLineSegment(sketch, "E98", {"start": v(2049.9, -760) * mm, "end": v(2303.79, -760) * mm});
            skLineSegment(sketch, "E99", {"start": v(2109.5, -720) * mm, "end": v(2303.79, -720) * mm});
            skLineSegment(sketch, "E100", {"start": v(2303.79, -760) * mm, "end": v(2303.79, -720) * mm});
            skLineSegment(sketch, "E101.MirrorCS", {"start": v(-1627.22, -240) * mm, "end": v(-1627.22, -280) * mm});
            skLineSegment(sketch, "E102.MirrorCS", {"start": v(-2303.79, -760) * mm, "end": v(-2303.79, -720) * mm});
            skLineSegment(sketch, "E103.MirrorCS", {"start": v(-2068.68, -760) * mm, "end": v(-2303.79, -760) * mm});
            skLineSegment(sketch, "E104.MirrorCS", {"start": v(-1627.22, -240) * mm, "end": v(-1879, -240) * mm});
            skLineSegment(sketch, "E105.MirrorCS", {"start": v(-1627.22, -280) * mm, "end": v(-1838.28, -280) * mm});
            skLineSegment(sketch, "E106.MirrorCS", {"start": v(-1838.28, -523.02) * mm, "end": v(-2068.68, -523.02) * mm});
            skLineSegment(sketch, "E107.MirrorCS", {"start": v(-2068.68, -523.02) * mm, "end": v(-2068.68, -760) * mm});
            skLineSegment(sketch, "E108.MirrorCS", {"start": v(-2110, -483.02) * mm, "end": v(-1878.26, -483.02) * mm});
            skLineSegment(sketch, "E109.MirrorCS", {"start": v(-1838.28, -280) * mm, "end": v(-1838.28, -523.02) * mm});
            skLineSegment(sketch, "E110.MirrorCS", {"start": v(-1879, -240) * mm, "end": v(-1878.26, -483.02) * mm});
            skLineSegment(sketch, "E111.MirrorCS", {"start": v(-2109.5, -720) * mm, "end": v(-2303.79, -720) * mm});
            skLineSegment(sketch, "E112.MirrorCS", {"start": v(-2109.5, -720) * mm, "end": v(-2110, -483.02) * mm});
            skSolve(sketch);
        }
        {
            var Q0;
            Q0=makeQuery(id+"F17.imprint","IMPRINT",FACE,{"disambiguationData":[TD([[makeQuery(id+"F17.imprint","IMPRINT",EDGE,{"derivedFrom":sQuery(id+"F17.wireOp",EDGE,"E87")}),1.0]])]});
            var Q1;
            Q1=makeQuery(id+"F17.imprint","IMPRINT",FACE,{"disambiguationData":[TD([[makeQuery(id+"F17.imprint","IMPRINT",EDGE,{"derivedFrom":sQuery(id+"F17.wireOp",EDGE,"E87")}),1.0]])]});
            var Q2;
            {var subQ5=sQuery(id+"F17.wireOp",EDGE,"E95");Q2=makeQuery(id+"F17.imprint","IMPRINT",FACE,{"disambiguationData":[TD([[makeQuery(id+"F17.imprint","IMPRINT",EDGE,{"derivedFrom":subQ5}),1.0]])]});}
            var Q3;
            Q3=makeQuery(id+"F17.imprint","IMPRINT",FACE,{"disambiguationData":[TD([[makeQuery(id+"F17.imprint","IMPRINT",EDGE,{"derivedFrom":sQuery(id+"F17.wireOp",EDGE,"E106.MirrorCS")}),-1.0]])]});
            extrude(context, id + "F18", {"entities" : qUnion([Q0, Q1, Q2, Q3]), "operationType" : NewBodyOperationType.ADD, "oppositeDirection" : true, "depth" : 40 * mm});
        }
        {
            var Q0;
            Q0=makeQuery(id+"F14.boolean.opBoolean","MERGE",FACE,{"derivedFrom":[makeQuery(id+"F10.boolean.opBoolean","MERGE",FACE,{"derivedFrom":[makeQuery(id+"F8.boolean.opBoolean","MERGE",FACE,{"derivedFrom":[makeQuery(id+"F6.boolean.opBoolean","MERGE",FACE,{"derivedFrom":[makeQuery(id+"F4.boolean.opBoolean","MERGE",FACE,{"derivedFrom":[makeQuery(id+"F3.boolean.opBoolean","MERGE",FACE,{"derivedFrom":[makeQuery(id+"F1.opExtrude","SWEPT_FACE",FACE,{"disambiguationData":[OSD([sQuery(id+"F0.wireOp",EDGE,"E0.rect.bottom")])]}),makeQuery(id+"F3.opExtrude","SWEPT_FACE",FACE,{"disambiguationData":[OSD([sQuery(id+"F2.wireOp",EDGE,"E15.bottom")])]}),makeQuery(id+"F3.opExtrude","SWEPT_FACE",FACE,{"disambiguationData":[OSD([sQuery(id+"F2.wireOp",EDGE,"E24.top")])]})]}),makeQuery(id+"F4.opExtrude","SWEPT_FACE",FACE,{"disambiguationData":[OSD([sQuery(id+"F2.wireOp",EDGE,"E19.top")])]}),makeQuery(id+"F4.opExtrude","SWEPT_FACE",FACE,{"disambiguationData":[OSD([sQuery(id+"F2.wireOp",EDGE,"E20.top")])]}),makeQuery(id+"F4.opExtrude","SWEPT_FACE",FACE,{"disambiguationData":[OSD([sQuery(id+"F2.wireOp",EDGE,"E21.top")])]})]}),makeQuery(id+"F6.opExtrude","SWEPT_FACE",FACE,{"disambiguationData":[OSD([sQuery(id+"F5.wireOp",EDGE,"E34.MirrorCS")])]})]}),makeQuery(id+"F8.opExtrude","SWEPT_FACE",FACE,{"disambiguationData":[OSD([sQuery(id+"F7.wireOp",EDGE,"E35.bottom")])]}),makeQuery(id+"F8.opExtrude","SWEPT_FACE",FACE,{"disambiguationData":[OSD([sQuery(id+"F7.wireOp",EDGE,"E43.MirrorCS")])]})]}),makeQuery(id+"F10.opExtrude","SWEPT_FACE",FACE,{"disambiguationData":[OSD([sQuery(id+"F9.wireOp",EDGE,"E45.bottom")])]}),makeQuery(id+"F10.opExtrude","SWEPT_FACE",FACE,{"disambiguationData":[OSD([sQuery(id+"F9.wireOp",EDGE,"E49.MirrorCS")])]})]}),makeQuery(id+"F14.opExtrude","SWEPT_FACE",FACE,{"disambiguationData":[OSD([sQuery(id+"F13.wireOp",EDGE,"E79.MirrorCS")])]})]});
            var sketch = newSketch(context, id + "F19", { "sketchPlane" : qUnion([Q0])});
            skLineSegment(sketch, "E113", {"start": v(-1650, 1004.2) * mm, "end": v(-2300, 260) * mm});
            skLineSegment(sketch, "E114", {"start": v(-1650, 1065) * mm, "end": v(-1650, 1004.2) * mm});
            skLineSegment(sketch, "E115.MirrorCS", {"start": v(1650, 1004.2) * mm, "end": v(2300, 260) * mm});
            skLineSegment(sketch, "E116.MirrorCS", {"start": v(1650, 1065) * mm, "end": v(1650, 1004.2) * mm});
            skLineSegment(sketch, "E117", {"start": v(-1650, 1065) * mm, "end": v(-2340, 275) * mm});
            skLineSegment(sketch, "E118", {"start": v(-2340, 275) * mm, "end": v(-2300, 260) * mm});
            skLineSegment(sketch, "E119.MirrorCS", {"start": v(1650, 1065) * mm, "end": v(2340, 275) * mm});
            skLineSegment(sketch, "E120.MirrorCS", {"start": v(2340, 275) * mm, "end": v(2300, 260) * mm});
            skSolve(sketch);
        }
        {
            var Q0;
            Q0 = qSketchRegion(id + "F19", true);
            var Q1;
            Q1=makeQuery(id+"F19.imprint","IMPRINT",FACE,{"disambiguationData":[TD([[makeQuery(id+"F19.imprint","IMPRINT",EDGE,{"derivedFrom":sQuery(id+"F19.wireOp",EDGE,"6684321e-4cf0-40c5-b09d-3aa0e726d688")}),1.0]])]});
            extrude(context, id + "F20", {"entities" : qUnion([Q0, Q1]), "operationType" : NewBodyOperationType.ADD, "oppositeDirection" : true, "depth" : 40 * mm});
        }
        {
            var Q0;
            {var subQ0=sQuery(id+"F2.wireOp",EDGE,"E28.MirrorCS");var subQ5=sQuery(id+"F2.wireOp",EDGE,"E27.MirrorCS");var subQ6=sQuery(id+"F2.wireOp",EDGE,"E29.MirrorCS");Q0=makeQuery(id+"F16.boolean.opBoolean","MERGE",FACE,{"derivedFrom":[makeQuery(id+"F3.boolean.opBoolean","SPLIT",FACE,{"disambiguationData":[TD([makeQuery(id+"F3.opExtrude","CAP_FACE",FACE,{"disambiguationData":[OSD([sQuery(id+"F2.wireOp",EDGE,"E26.MirrorCS"),subQ5,subQ0,subQ6])],"isStart":false})])],"derivedFrom":makeQuery(id+"F3.opExtrude","SWEPT_FACE",FACE,{"disambiguationData":[OSD([subQ0])]})}),makeQuery(id+"F16.opExtrude","SWEPT_FACE",FACE,{"disambiguationData":[OSD([sQuery(id+"F15.wireOp",EDGE,"E80.bottom")])]})]});}
            var sketch = newSketch(context, id + "F21", { "sketchPlane" : qUnion([Q0])});
            skLineSegment(sketch, "E121", {"start": v(-1650, 1065) * mm, "end": v(-2340, 275.01) * mm});
            skLineSegment(sketch, "E122", {"start": v(-1635.9, 1020.35) * mm, "end": v(-2333.6, 221.54) * mm});
            skLineSegment(sketch, "E123", {"start": v(-2340, 275.01) * mm, "end": v(-2333.6, 221.54) * mm});
            skLineSegment(sketch, "E124", {"start": v(-1650, 1065) * mm, "end": v(-1635.9, 1020.35) * mm});
            skLineSegment(sketch, "E125.MirrorCS", {"start": v(1635.9, 1020.35) * mm, "end": v(2333.6, 221.54) * mm});
            skLineSegment(sketch, "E126.MirrorCS", {"start": v(1650, 1065) * mm, "end": v(2340, 275.01) * mm});
            skLineSegment(sketch, "E127.MirrorCS", {"start": v(2340, 275.01) * mm, "end": v(2333.6, 221.54) * mm});
            skLineSegment(sketch, "E128.MirrorCS", {"start": v(1650, 1065) * mm, "end": v(1635.9, 1020.35) * mm});
            skSolve(sketch);
        }
        {
            var Q0;
            {var subQ7=sQuery(id+"F21.wireOp",EDGE,"E121");Q0=makeQuery(id+"F21.imprint","IMPRINT",FACE,{"disambiguationData":[TD([[makeQuery(id+"F21.imprint","IMPRINT",EDGE,{"derivedFrom":subQ7}),1.0]])]});}
            var Q1;
            Q1=makeQuery(id+"F21.imprint","IMPRINT",FACE,{"disambiguationData":[TD([[makeQuery(id+"F21.imprint","IMPRINT",EDGE,{"derivedFrom":sQuery(id+"F21.wireOp",EDGE,"E125.MirrorCS")}),1.0]])]});
            extrude(context, id + "F22", {"entities" : qUnion([Q0, Q1]), "operationType" : NewBodyOperationType.ADD, "oppositeDirection" : true, "depth" : 40 * mm});
        }
        {
            var Q0;
            {var subQ0=sQuery(id+"F0.wireOp",EDGE,"E0.rect.bottom");var subQ1=sQuery(id+"F2.wireOp",EDGE,"E24.top");var subQ2=sQuery(id+"F5.wireOp",EDGE,"E34.MirrorCS");var subQ3=sQuery(id+"F7.wireOp",EDGE,"E35.bottom");var subQ4=sQuery(id+"F9.wireOp",EDGE,"E45.bottom");var subQ5=sQuery(id+"F9.wireOp",EDGE,"E49.MirrorCS");Q0=makeQuery(id+"F20.boolean.opBoolean","MERGE",FACE,{"derivedFrom":[makeQuery(id+"F18.boolean.opBoolean","MERGE",FACE,{"derivedFrom":[makeQuery(id+"F14.boolean.opBoolean","MERGE",FACE,{"derivedFrom":[makeQuery(id+"F10.boolean.opBoolean","MERGE",FACE,{"derivedFrom":[makeQuery(id+"F8.boolean.opBoolean","MERGE",FACE,{"derivedFrom":[makeQuery(id+"F6.boolean.opBoolean","MERGE",FACE,{"derivedFrom":[makeQuery(id+"F4.boolean.opBoolean","MERGE",FACE,{"derivedFrom":[makeQuery(id+"F3.boolean.opBoolean","MERGE",FACE,{"derivedFrom":[makeQuery(id+"F1.opExtrude","SWEPT_FACE",FACE,{"disambiguationData":[OSD([subQ0])]}),makeQuery(id+"F3.opExtrude","SWEPT_FACE",FACE,{"disambiguationData":[OSD([sQuery(id+"F2.wireOp",EDGE,"E15.bottom")])]}),makeQuery(id+"F3.opExtrude","SWEPT_FACE",FACE,{"disambiguationData":[OSD([subQ1])]})]}),makeQuery(id+"F4.opExtrude","SWEPT_FACE",FACE,{"disambiguationData":[OSD([sQuery(id+"F2.wireOp",EDGE,"E19.top")])]}),makeQuery(id+"F4.opExtrude","SWEPT_FACE",FACE,{"disambiguationData":[OSD([sQuery(id+"F2.wireOp",EDGE,"E20.top")])]}),makeQuery(id+"F4.opExtrude","SWEPT_FACE",FACE,{"disambiguationData":[OSD([sQuery(id+"F2.wireOp",EDGE,"E21.top")])]})]}),makeQuery(id+"F6.opExtrude","SWEPT_FACE",FACE,{"disambiguationData":[OSD([subQ2])]})]}),makeQuery(id+"F8.opExtrude","SWEPT_FACE",FACE,{"disambiguationData":[OSD([subQ3])]}),makeQuery(id+"F8.opExtrude","SWEPT_FACE",FACE,{"disambiguationData":[OSD([sQuery(id+"F7.wireOp",EDGE,"E43.MirrorCS")])]})]}),makeQuery(id+"F10.opExtrude","SWEPT_FACE",FACE,{"disambiguationData":[OSD([subQ4])]}),makeQuery(id+"F10.opExtrude","SWEPT_FACE",FACE,{"disambiguationData":[OSD([subQ5])]})]}),makeQuery(id+"F14.opExtrude","SWEPT_FACE",FACE,{"disambiguationData":[OSD([sQuery(id+"F13.wireOp",EDGE,"E79.MirrorCS")])]})]}),makeQuery(id+"F18.opExtrude","CAP_FACE",FACE,{"disambiguationData":[OSD([subQ3,subQ4,sQuery(id+"F9.wireOp",EDGE,"E45.right"),sQuery(id+"F17.wireOp",EDGE,"E86"),sQuery(id+"F17.wireOp",EDGE,"E87"),sQuery(id+"F17.wireOp",EDGE,"E88"),sQuery(id+"F17.wireOp",EDGE,"E89"),sQuery(id+"F17.wireOp",EDGE,"E90"),sQuery(id+"F17.wireOp",EDGE,"E91"),sQuery(id+"F17.wireOp",EDGE,"E92"),sQuery(id+"F17.wireOp",EDGE,"E94"),sQuery(id+"F17.wireOp",EDGE,"E95"),sQuery(id+"F17.wireOp",EDGE,"E98"),sQuery(id+"F17.wireOp",EDGE,"E99")])],"isStart":true}),makeQuery(id+"F18.opExtrude","CAP_FACE",FACE,{"disambiguationData":[OSD([subQ0,sQuery(id+"F0.wireOp",EDGE,"E0.rect.left"),subQ1,sQuery(id+"F2.wireOp",EDGE,"E24.right"),subQ2,subQ5,sQuery(id+"F9.wireOp",EDGE,"E50.MirrorCS"),sQuery(id+"F17.wireOp",EDGE,"E103.MirrorCS"),sQuery(id+"F17.wireOp",EDGE,"E104.MirrorCS"),sQuery(id+"F17.wireOp",EDGE,"E105.MirrorCS"),sQuery(id+"F17.wireOp",EDGE,"E106.MirrorCS"),sQuery(id+"F17.wireOp",EDGE,"E107.MirrorCS"),sQuery(id+"F17.wireOp",EDGE,"E108.MirrorCS"),sQuery(id+"F17.wireOp",EDGE,"E109.MirrorCS"),sQuery(id+"F17.wireOp",EDGE,"E110.MirrorCS"),sQuery(id+"F17.wireOp",EDGE,"E111.MirrorCS"),sQuery(id+"F17.wireOp",EDGE,"E112.MirrorCS")])],"isStart":true})]}),makeQuery(id+"F20.opExtrude","CAP_FACE",FACE,{"disambiguationData":[OSD([sQuery(id+"F19.wireOp",EDGE,"E113"),sQuery(id+"F19.wireOp",EDGE,"E114"),sQuery(id+"F19.wireOp",EDGE,"E117"),sQuery(id+"F19.wireOp",EDGE,"E118")])],"isStart":true}),makeQuery(id+"F20.opExtrude","CAP_FACE",FACE,{"disambiguationData":[OSD([sQuery(id+"F19.wireOp",EDGE,"E115.MirrorCS"),sQuery(id+"F19.wireOp",EDGE,"E116.MirrorCS"),sQuery(id+"F19.wireOp",EDGE,"E119.MirrorCS"),sQuery(id+"F19.wireOp",EDGE,"E120.MirrorCS")])],"isStart":true})]});}
            var sketch = newSketch(context, id + "F23", { "sketchPlane" : qUnion([Q0])});
            skCircle(sketch, "E129", {"center": v(-2220, -995) * mm, "radius": 15 * mm});
            skCircle(sketch, "E130.MirrorC", {"center": v(2220, -995) * mm, "radius": 15 * mm});
            skSolve(sketch);
        }
        {
            var Q0;
            Q0=makeQuery(id+"F23.imprint","IMPRINT",FACE,{"disambiguationData":[TD([[makeQuery(id+"F23.imprint","IMPRINT",EDGE,{"derivedFrom":sQuery(id+"F23.wireOp",EDGE,"E130.MirrorC")}),-1.0]])]});
            var Q1;
            Q1=makeQuery(id+"F23.imprint","IMPRINT",FACE,{"disambiguationData":[TD([[makeQuery(id+"F23.imprint","IMPRINT",EDGE,{"derivedFrom":sQuery(id+"F23.wireOp",EDGE,"E129")}),1.0]])]});
            extrude(context, id + "F24", {"entities" : qUnion([Q0, Q1]), "operationType" : NewBodyOperationType.REMOVE, "endBound" : BoundingType.THROUGH_ALL, "oppositeDirection" : true, "depth" : 25 * mm});
        }
    });
